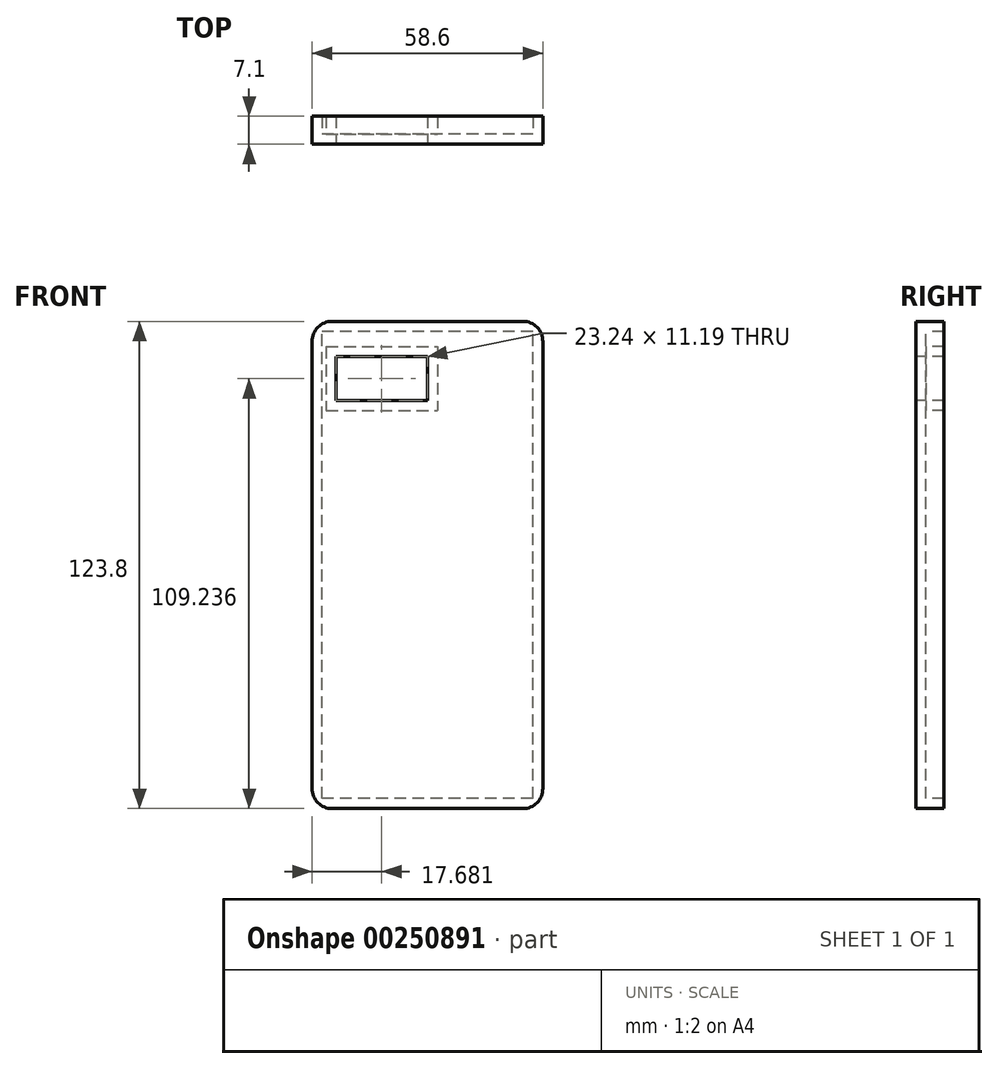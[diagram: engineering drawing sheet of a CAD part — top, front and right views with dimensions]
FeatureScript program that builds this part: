
annotation { "Feature Type Name" : "Feature", "Feature Type Description" : "" }
export const myFeature = defineFeature(function(context is Context, id is Id, definition is map)
    precondition{}
    {
        {
            var Q0;
            Q0=qCreatedBy(makeId("Front.planeOp"),FACE);
            var sketch = newSketch(context, id + "F0", { "sketchPlane" : qUnion([Q0])});
            skLineSegment(sketch, "E0.bottom", {"start": v(29.3, -61.9) * mm, "end": v(-29.3, -61.9) * mm});
            skLineSegment(sketch, "E0.top", {"start": v(29.3, 61.9) * mm, "end": v(-29.3, 61.9) * mm});
            skLineSegment(sketch, "E0.left", {"start": v(29.3, -61.9) * mm, "end": v(29.3, 61.9) * mm});
            skLineSegment(sketch, "E0.right", {"start": v(-29.3, -61.9) * mm, "end": v(-29.3, 61.9) * mm});
            skPoint(sketch, "E0.middle", {"position": v(0, 0) * mm});
            skLineSegment(sketch, "E1.bottom", {"start": v(-23.24, 52.93) * mm, "end": v(0, 52.93) * mm});
            skLineSegment(sketch, "E1.top", {"start": v(-23.24, 41.74) * mm, "end": v(0, 41.74) * mm});
            skLineSegment(sketch, "E1.left", {"start": v(-23.24, 52.93) * mm, "end": v(-23.24, 41.74) * mm});
            skLineSegment(sketch, "E1.right", {"start": v(0, 52.93) * mm, "end": v(0, 41.74) * mm});
            skSolve(sketch);
        }
        {
            var Q0;
            Q0 = qSketchRegion(id + "F0", true);
            extrude(context, id + "F1", {"entities" : qUnion([Q0]), "endBound" : BoundingType.SYMMETRIC, "oppositeDirection" : true, "depth" : 7.1 * mm});
        }
        {
            var Q0;
            Q0=makeQuery(id+"F1.opExtrude","CAP_FACE",FACE,{"disambiguationData":[OSD([sQuery(id+"F0.wireOp",EDGE,"E0.bottom"),sQuery(id+"F0.wireOp",EDGE,"E0.top"),sQuery(id+"F0.wireOp",EDGE,"E0.left"),sQuery(id+"F0.wireOp",EDGE,"E0.right")])],"isStart":false});
            shell(context, id + "F2", {"entities" : qUnion([Q0]), "thickness" : 2.54 * mm});
        }
        {
            var Q0;
            Q0=makeQuery(id+"F1.opExtrude","SWEPT_EDGE",EDGE,{"disambiguationData":[OSD([sQuery(id+"F0.wireOp",EDGE,"E0.top"),sQuery(id+"F0.wireOp",EDGE,"E0.left")])]});
            var Q1;
            Q1=makeQuery(id+"F1.opExtrude","SWEPT_EDGE",EDGE,{"disambiguationData":[OSD([sQuery(id+"F0.wireOp",EDGE,"E0.top"),sQuery(id+"F0.wireOp",EDGE,"E0.right")])]});
            var Q2;
            Q2=makeQuery(id+"F1.opExtrude","SWEPT_EDGE",EDGE,{"disambiguationData":[OSD([sQuery(id+"F0.wireOp",EDGE,"E0.bottom"),sQuery(id+"F0.wireOp",EDGE,"E0.left")])]});
            var Q3;
            Q3=makeQuery(id+"F1.opExtrude","SWEPT_EDGE",EDGE,{"disambiguationData":[OSD([sQuery(id+"F0.wireOp",EDGE,"E0.bottom"),sQuery(id+"F0.wireOp",EDGE,"E0.right")])]});
            fillet(context, id + "F3", {"entities" : qUnion([Q0, Q1, Q2, Q3]), "radius" : 5.08 * mm, "tangentPropagation" : true, "allowEdgeOverflow" : false});
        }
    });
